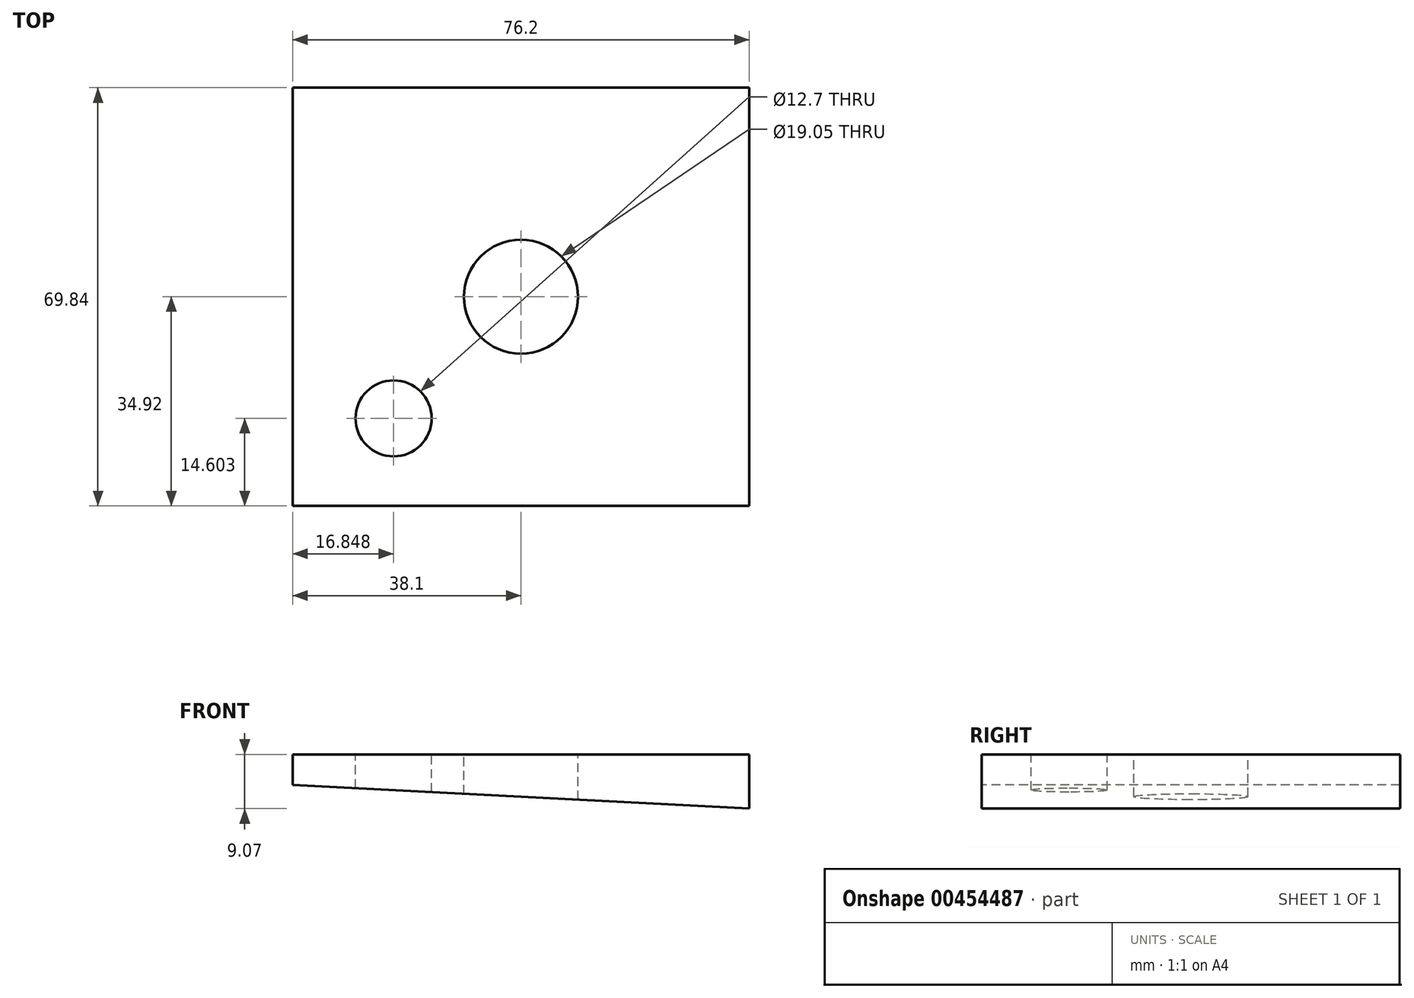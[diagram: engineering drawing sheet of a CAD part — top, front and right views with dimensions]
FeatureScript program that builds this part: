
annotation { "Feature Type Name" : "Feature", "Feature Type Description" : "" }
export const myFeature = defineFeature(function(context is Context, id is Id, definition is map)
    precondition{}
    {
        {
            var Q0;
            Q0=qCreatedBy(makeId("Top.planeOp"),FACE);
            var sketch = newSketch(context, id + "F0", { "sketchPlane" : qUnion([Q0])});
            skLineSegment(sketch, "E0.bottom", {"start": v(-38.1, 34.93) * mm, "end": v(38.1, 34.93) * mm});
            skLineSegment(sketch, "E0.top", {"start": v(-38.1, -34.93) * mm, "end": v(38.1, -34.93) * mm});
            skLineSegment(sketch, "E0.left", {"start": v(-38.1, 34.93) * mm, "end": v(-38.1, -34.92) * mm});
            skLineSegment(sketch, "E0.right", {"start": v(38.1, 34.93) * mm, "end": v(38.1, -34.92) * mm});
            skPoint(sketch, "E0.middle", {"position": v(0, 0) * mm});
            skCircle(sketch, "E1", {"center": v(-21.25, -20.32) * mm, "radius": 6.35 * mm});
            skSolve(sketch);
        }
        {
            var Q0;
            Q0=makeQuery(id+"F0.imprint","IMPRINT",FACE,{"disambiguationData":[TD([[makeQuery(id+"F0.imprint","IMPRINT",EDGE,{"derivedFrom":sQuery(id+"F0.wireOp",EDGE,"E0.bottom")}),-1.0]])]});
            extrude(context, id + "F1", {"entities" : qUnion([Q0]), "oppositeDirection" : true, "depth" : 5.08 * mm});
        }
        {
            var Q0;
            Q0=makeQuery(id+"F1.opExtrude","SWEPT_FACE",FACE,{"disambiguationData":[OSD([sQuery(id+"F0.wireOp",EDGE,"E0.top")])]});
            var sketch = newSketch(context, id + "F2", { "sketchPlane" : qUnion([Q0])});
            skLineSegment(sketch, "E2", {"start": v(-38.1, 0) * mm, "end": v(38.2, 4) * mm});
            skLineSegment(sketch, "E3", {"start": v(38.1, 0) * mm, "end": v(38.2, 4) * mm});
            skLineSegment(sketch, "E4", {"start": v(38.1, -5.08) * mm, "end": v(38.1, -9.07) * mm});
            skLineSegment(sketch, "E5", {"start": v(-38.1, -5.08) * mm, "end": v(38.1, -9.07) * mm});
            skSolve(sketch);
        }
        {
            var Q0;
            Q0=makeQuery(id+"F2.imprint","IMPRINT",FACE,{"disambiguationData":[TD([[makeQuery(id+"F2.imprint","IMPRINT",EDGE,{"derivedFrom":sQuery(id+"F2.wireOp",EDGE,"E4")}),-1.0]])]});
            extrude(context, id + "F3", {"entities" : qUnion([Q0]), "operationType" : NewBodyOperationType.ADD, "oppositeDirection" : true, "depth" : 69.85 * mm});
        }
        {
            var Q0;
            Q0=sQuery(id+"F0.wireOp",VERTEX,"E0.middle");
            var Q1;
            Q1=makeQuery(id+"F1.opExtrude","SWEPT_BODY",BODY,{"disambiguationData":[OSD([sQuery(id+"F0.wireOp",EDGE,"E0.bottom"),sQuery(id+"F0.wireOp",EDGE,"E0.top"),sQuery(id+"F0.wireOp",EDGE,"E0.left"),sQuery(id+"F0.wireOp",EDGE,"E0.right"),sQuery(id+"F0.wireOp",EDGE,"E1")])]});
            hole(context, id + "F4", {"style" : HoleStyle.SIMPLE, "endStyle" : HoleEndStyle.BLIND, "holeDiameter" : 19.05 * mm, "holeDepth" : 25.4 * mm, "isTappedThrough" : true, "tappedDepth" : 12.7 * mm, "tapClearance" : 3, "startFromSketch" : true, "locations" : qUnion([Q0]), "scope" : qUnion([Q1])});
        }
        {
            var Q0;
            Q0=sQuery(id+"F0.wireOp",VERTEX,"E1.center");
            var Q1;
            Q1=makeQuery(id+"F1.opExtrude","SWEPT_BODY",BODY,{"disambiguationData":[OSD([sQuery(id+"F0.wireOp",EDGE,"E0.bottom"),sQuery(id+"F0.wireOp",EDGE,"E0.top"),sQuery(id+"F0.wireOp",EDGE,"E0.left"),sQuery(id+"F0.wireOp",EDGE,"E0.right"),sQuery(id+"F0.wireOp",EDGE,"E1")])]});
            hole(context, id + "F5", {"style" : HoleStyle.SIMPLE, "endStyle" : HoleEndStyle.BLIND, "holeDiameter" : 12.7 * mm, "holeDepth" : 25.4 * mm, "isTappedThrough" : true, "tappedDepth" : 12.7 * mm, "tapClearance" : 3, "startFromSketch" : true, "locations" : qUnion([Q0]), "scope" : qUnion([Q1])});
        }
    });
